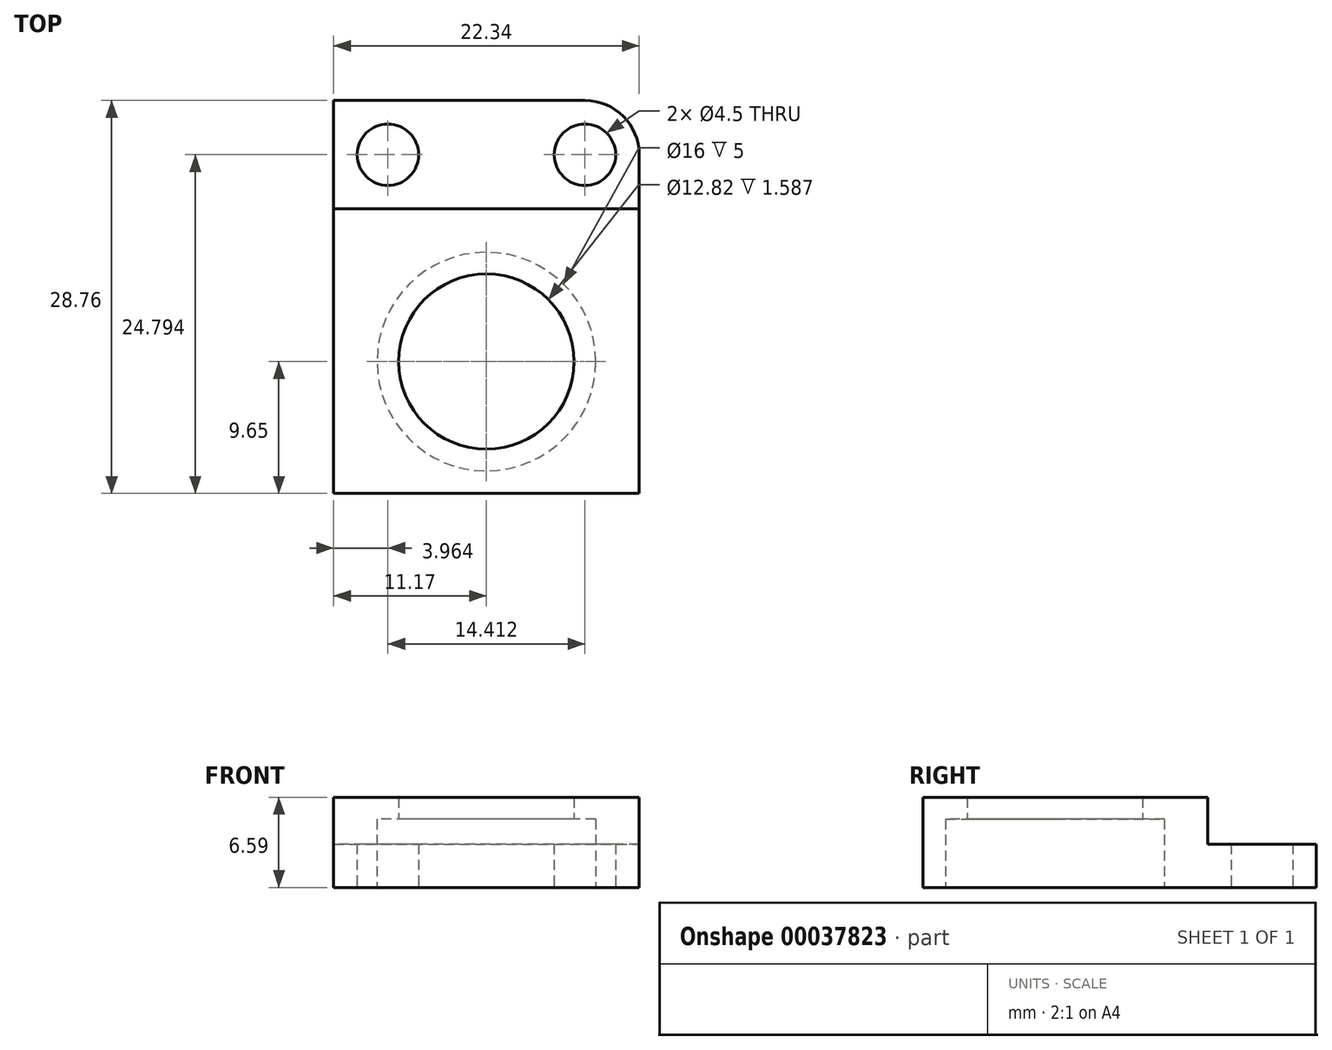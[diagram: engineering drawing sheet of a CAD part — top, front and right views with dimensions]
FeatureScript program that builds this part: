
annotation { "Feature Type Name" : "Feature", "Feature Type Description" : "" }
export const myFeature = defineFeature(function(context is Context, id is Id, definition is map)
    precondition{}
    {
        {
            var Q0;
            Q0=qCreatedBy(makeId("Top.planeOp"),FACE);
            var sketch = newSketch(context, id + "F0", { "sketchPlane" : qUnion([Q0])});
            skLineSegment(sketch, "E0", {"start": v(0, 0) * mm, "end": v(0, 9.65) * mm, "construction": true});
            skLineSegment(sketch, "E1", {"start": v(0, 9.65) * mm, "end": v(0, 28.76) * mm, "construction": true});
            skLineSegment(sketch, "E2", {"start": v(11.17, 0) * mm, "end": v(-11.17, 0) * mm});
            skLineSegment(sketch, "E3", {"start": v(-11.17, 0) * mm, "end": v(-11.17, 28.76) * mm});
            skLineSegment(sketch, "E4", {"start": v(11.17, 0) * mm, "end": v(11.17, 28.76) * mm});
            skLineSegment(sketch, "E5", {"start": v(11.17, 28.76) * mm, "end": v(-11.17, 28.76) * mm});
            skCircle(sketch, "E6", {"center": v(7.2, 24.8) * mm, "radius": 3.97 * mm, "construction": true});
            skLineSegment(sketch, "E7", {"start": v(7.2, 24.8) * mm, "end": v(-7.2, 24.8) * mm, "construction": true});
            skPoint(sketch, "E8", {"position": v(0, 24.8) * mm});
            skCircle(sketch, "E9", {"center": v(-7.2, 24.8) * mm, "radius": 2.25 * mm});
            skCircle(sketch, "E10", {"center": v(7.2, 24.8) * mm, "radius": 2.25 * mm});
            skCircle(sketch, "E11", {"center": v(0, 9.65) * mm, "radius": 8 * mm});
            skSolve(sketch);
        }
        {
            var Q0;
            Q0=qSketchRegion(id+"F0",true);
            extrude(context, id + "F1", {"entities" : qUnion([Q0]), "depth" : 3.17 * mm});
        }
        {
            var Q0;
            Q0=makeQuery(id+"F1.opExtrude","CAP_FACE",FACE,{"disambiguationData":[OSD([sQuery(id+"F0.wireOp",EDGE,"cd2821f5-4831-4a1e-b02c-f6531e8d6a60"),sQuery(id+"F0.wireOp",EDGE,"f5fb9684-6b33-4355-9c5c-313f103c1c62"),sQuery(id+"F0.wireOp",EDGE,"ad4d735d-fb8e-4b7d-bd62-e2e4cd1506b4"),sQuery(id+"F0.wireOp",EDGE,"E2"),sQuery(id+"F0.wireOp",EDGE,"E3"),sQuery(id+"F0.wireOp",EDGE,"1d698fc5-a467-472c-b147-6fd77103e892"),sQuery(id+"F0.wireOp",EDGE,"E4"),sQuery(id+"F0.wireOp",EDGE,"E5"),sQuery(id+"F0.wireOp",EDGE,"E9"),sQuery(id+"F0.wireOp",EDGE,"E10")])],"isStart":false});
            var sketch = newSketch(context, id + "F2", { "sketchPlane" : qUnion([Q0])});
            skLineSegment(sketch, "E12.bottom", {"start": v(-11.17, 0) * mm, "end": v(11.17, 0) * mm});
            skLineSegment(sketch, "E12.top", {"start": v(-11.17, 20.83) * mm, "end": v(11.17, 20.83) * mm});
            skLineSegment(sketch, "E12.left", {"start": v(-11.17, 0) * mm, "end": v(-11.17, 20.83) * mm});
            skLineSegment(sketch, "E12.right", {"start": v(11.17, 0) * mm, "end": v(11.17, 20.83) * mm});
            skCircle(sketch, "E13", {"center": v(0, 9.65) * mm, "radius": 8 * mm});
            skSolve(sketch);
        }
        {
            var Q0;
            Q0=qSketchRegion(id+"F2",true);
            extrude(context, id + "F3", {"entities" : qUnion([Q0]), "operationType" : NewBodyOperationType.ADD, "depth" : 1.82 * mm});
        }
        {
            var Q0;
            Q0=makeQuery(id+"F3.opExtrude","CAP_FACE",FACE,{"disambiguationData":[OSD([sQuery(id+"F2.wireOp",EDGE,"E12.bottom"),sQuery(id+"F2.wireOp",EDGE,"E12.top"),sQuery(id+"F2.wireOp",EDGE,"E12.left"),sQuery(id+"F2.wireOp",EDGE,"E12.right"),sQuery(id+"F2.wireOp",EDGE,"E13")])],"isStart":false});
            var sketch = newSketch(context, id + "F4", { "sketchPlane" : qUnion([Q0])});
            skCircle(sketch, "E14", {"center": v(0, 9.65) * mm, "radius": 6.41 * mm});
            skLineSegment(sketch, "E15.bottom", {"start": v(-11.17, 0) * mm, "end": v(11.17, 0) * mm});
            skLineSegment(sketch, "E15.top", {"start": v(-11.17, 20.83) * mm, "end": v(11.17, 20.83) * mm});
            skLineSegment(sketch, "E15.left", {"start": v(-11.17, 0) * mm, "end": v(-11.17, 20.83) * mm});
            skLineSegment(sketch, "E15.right", {"start": v(11.17, 0) * mm, "end": v(11.17, 20.83) * mm});
            skSolve(sketch);
        }
        {
            var Q0;
            Q0=makeQuery(id+"F4.imprint","IMPRINT",FACE,{"disambiguationData":[TD([[makeQuery(id+"F4.imprint","IMPRINT",EDGE,{"derivedFrom":sQuery(id+"F4.wireOp",EDGE,"E15.top")}),-1.0]])]});
            var Q1;
            Q1=makeQuery(id+"F4.imprint","IMPRINT",FACE,{"disambiguationData":[TD([[makeQuery(id+"F4.imprint","IMPRINT",EDGE,{"derivedFrom":sQuery(id+"F4.wireOp",EDGE,"E14")}),-1.0]])]});
            extrude(context, id + "F5", {"entities" : qUnion([Q0, Q1]), "operationType" : NewBodyOperationType.ADD, "depth" : 1.59 * mm});
        }
        {
            var Q0;
            Q0=makeQuery(id+"F1.opExtrude","SWEPT_EDGE",EDGE,{"disambiguationData":[OSD([sQuery(id+"F0.wireOp",EDGE,"E4"),sQuery(id+"F0.wireOp",EDGE,"E5")])]});
            fillet(context, id + "F6", {"entities" : qUnion([Q0]), "radius" : 3.97 * mm, "tangentPropagation" : true, "allowEdgeOverflow" : false});
        }
    });
